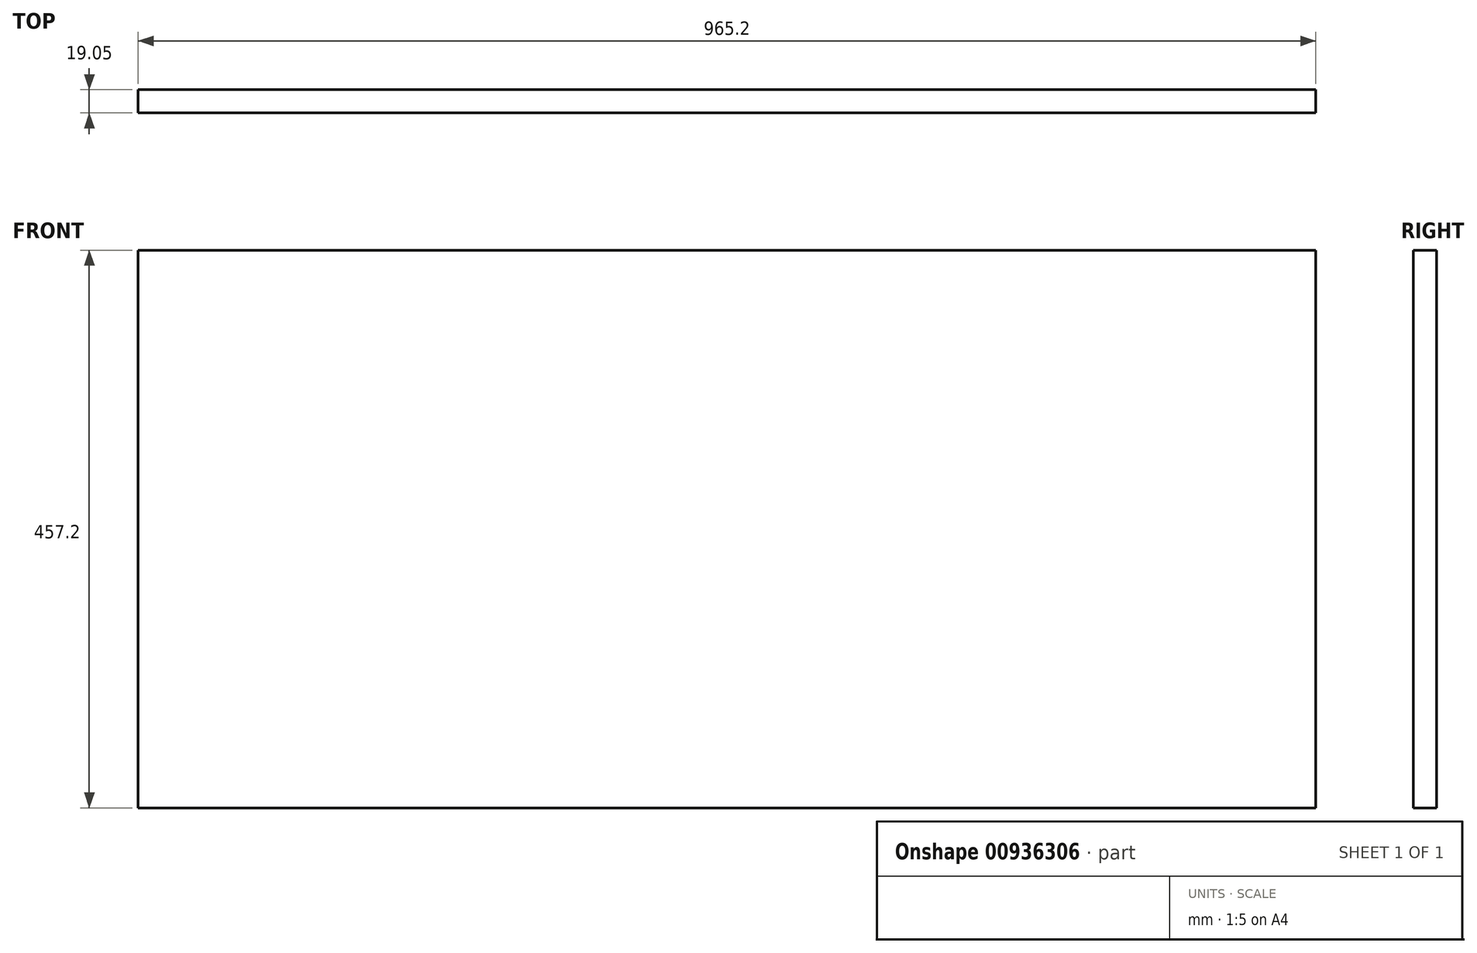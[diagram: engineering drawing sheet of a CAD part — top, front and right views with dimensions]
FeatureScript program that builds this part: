
annotation { "Feature Type Name" : "Feature", "Feature Type Description" : "" }
export const myFeature = defineFeature(function(context is Context, id is Id, definition is map)
    precondition{}
    {
        {
            var Q0;
            Q0=qCreatedBy(makeId("Front.planeOp"),FACE);
            var sketch = newSketch(context, id + "F0", { "sketchPlane" : qUnion([Q0])});
            skLineSegment(sketch, "E0.bottom", {"start": v(-455.45, 313.07) * mm, "end": v(509.75, 313.07) * mm});
            skLineSegment(sketch, "E0.top", {"start": v(-455.45, -144.13) * mm, "end": v(509.75, -144.13) * mm});
            skLineSegment(sketch, "E0.left", {"start": v(-455.45, 313.07) * mm, "end": v(-455.45, -144.13) * mm});
            skLineSegment(sketch, "E0.right", {"start": v(509.75, 313.07) * mm, "end": v(509.75, -144.13) * mm});
            skPoint(sketch, "E0.middle", {"position": v(27.15, 84.47) * mm});
            skSolve(sketch);
        }
        {
            var Q0;
            Q0=makeQuery(id+"F0.imprint","IMPRINT",FACE,{"disambiguationData":[TD([[makeQuery(id+"F0.imprint","IMPRINT",EDGE,{"derivedFrom":sQuery(id+"F0.wireOp",EDGE,"E0.bottom")}),-1.0]])]});
            extrude(context, id + "F1", {"entities" : qUnion([Q0]), "depth" : 19.05 * mm, "offsetDistance" : 25.4 * mm});
        }
    });
